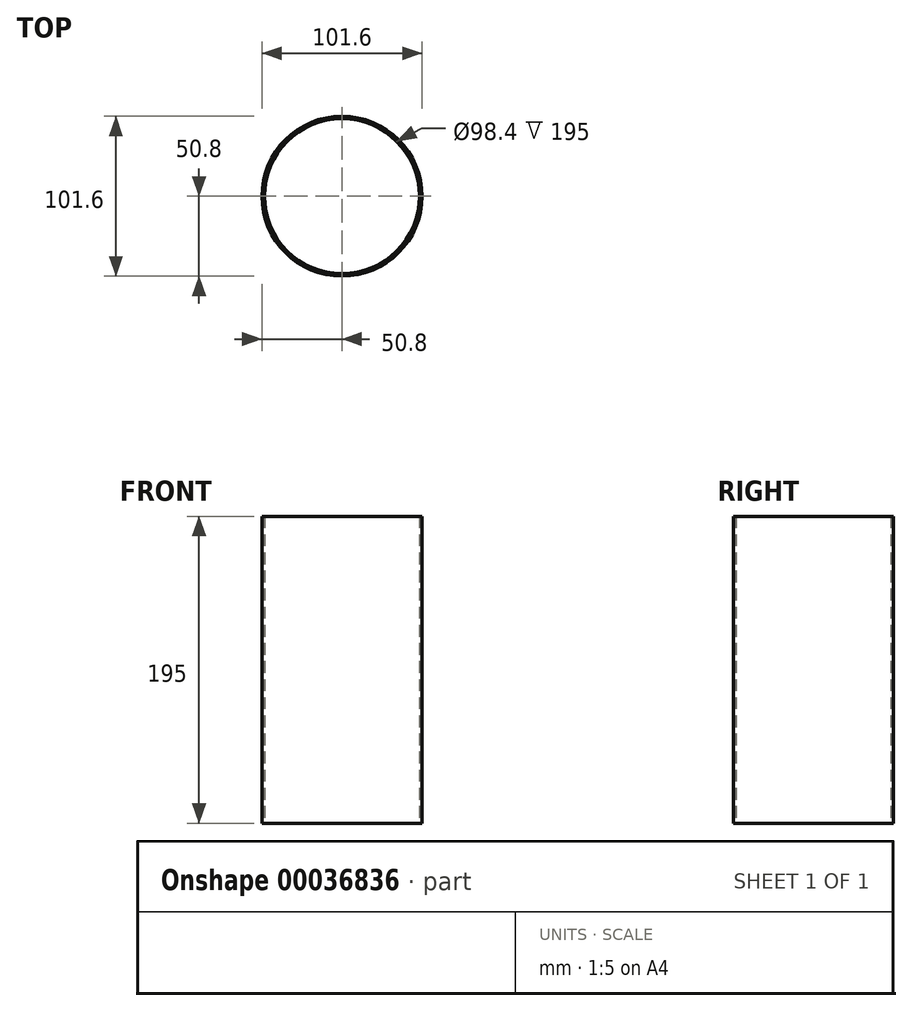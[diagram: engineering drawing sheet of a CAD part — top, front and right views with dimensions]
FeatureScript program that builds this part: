
annotation { "Feature Type Name" : "Feature", "Feature Type Description" : "" }
export const myFeature = defineFeature(function(context is Context, id is Id, definition is map)
    precondition{}
    {
        {
            var Q0;
            Q0=qCreatedBy(makeId("Top.planeOp"),FACE);
            var sketch = newSketch(context, id + "F0", { "sketchPlane" : qUnion([Q0])});
            skCircle(sketch, "E0", {"center": v(0, 0) * mm, "radius": 50.8 * mm});
            skCircle(sketch, "E1", {"center": v(0, 0) * mm, "radius": 49.2 * mm});
            skSolve(sketch);
        }
        {
            var Q0;
            Q0 = qSketchRegion(id + "F0", true);
            extrude(context, id + "F1", {"entities" : qUnion([Q0]), "depth" : 195 * mm});
        }
    });
